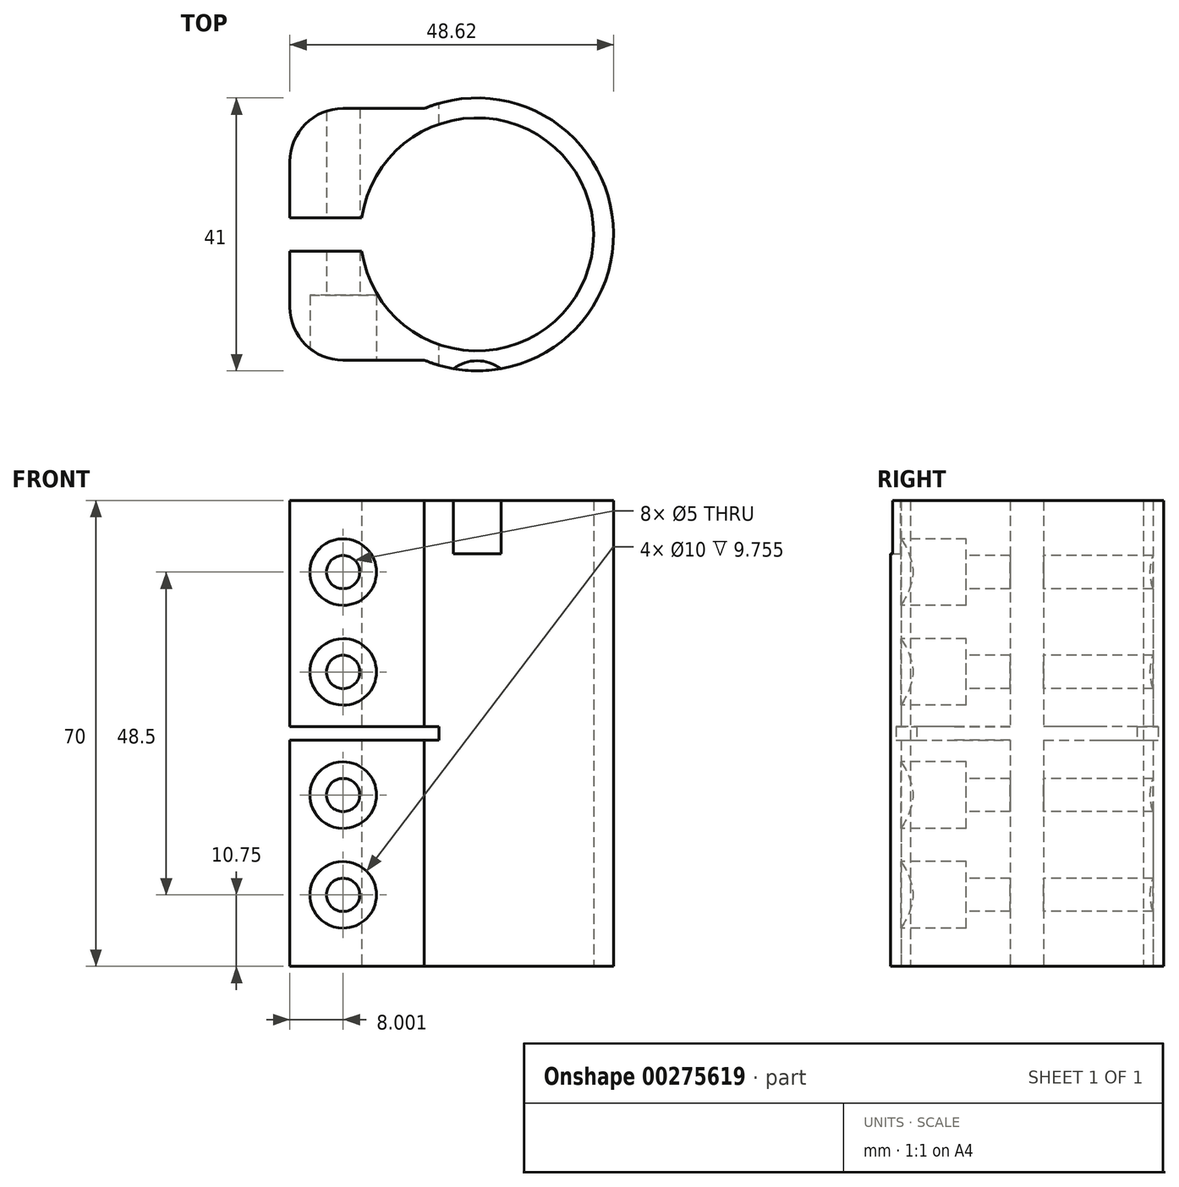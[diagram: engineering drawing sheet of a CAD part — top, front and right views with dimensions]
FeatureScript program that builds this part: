
annotation { "Feature Type Name" : "Feature", "Feature Type Description" : "" }
export const myFeature = defineFeature(function(context is Context, id is Id, definition is map)
    precondition{}
    {
        {
            var Q0;
            Q0=qCreatedBy(makeId("Top.planeOp"),FACE);
            var sketch = newSketch(context, id + "F0", { "sketchPlane" : qUnion([Q0])});
            skPoint(sketch, "E0", {"position": v(0, 0) * mm});
            skArc(sketch, "E1", {"start": v(-17.32, -2.5) * mm, "mid": v(17.5, 0) * mm, "end": v(-17.32, 2.5) * mm});
            skArc(sketch, "E2", {"start": v(-7.92, -18.9) * mm, "mid": v(20.5, 0) * mm, "end": v(-7.92, 18.9) * mm});
            skLineSegment(sketch, "E3", {"start": v(-7.92, 18.9) * mm, "end": v(-20.12, 18.9) * mm});
            skLineSegment(sketch, "E4", {"start": v(-28.12, 10.9) * mm, "end": v(-28.12, 2.5) * mm});
            skLineSegment(sketch, "E5", {"start": v(-28.12, 2.5) * mm, "end": v(-17.32, 2.5) * mm});
            skPoint(sketch, "E6.visualSharp", {"position": v(-28.12, 18.9) * mm});
            skArc(sketch, "E6.filletArc", {"start": v(-20.12, 18.9) * mm, "mid": v(-25.78, 16.57) * mm, "end": v(-28.12, 10.9) * mm});
            skLineSegment(sketch, "E7", {"start": v(0, 0) * mm, "end": v(48.76, 0) * mm, "construction": true});
            skLineSegment(sketch, "E8.MirrorCS", {"start": v(-7.92, -18.9) * mm, "end": v(-20.12, -18.9) * mm});
            skArc(sketch, "E9.MirrorCS", {"start": v(-20.12, -18.9) * mm, "mid": v(-25.78, -16.57) * mm, "end": v(-28.12, -10.9) * mm});
            skLineSegment(sketch, "E10.MirrorCS", {"start": v(-28.12, -10.9) * mm, "end": v(-28.12, -2.5) * mm});
            skLineSegment(sketch, "E11.MirrorCS", {"start": v(-28.12, -2.5) * mm, "end": v(-17.32, -2.5) * mm});
            skSolve(sketch);
        }
        {
            var Q0;
            Q0=qSketchRegion(id+"F0",true);
            extrude(context, id + "F1", {"entities" : qUnion([Q0]), "endBound" : BoundingType.SYMMETRIC, "depth" : 70 * mm});
        }
        {
            var Q0;
            Q0=makeQuery(id+"F1.opExtrude","SWEPT_FACE",FACE,{"disambiguationData":[OSD([sQuery(id+"F0.wireOp",EDGE,"E8.MirrorCS")])]});
            var sketch = newSketch(context, id + "F2", { "sketchPlane" : qUnion([Q0])});
            skPoint(sketch, "E12", {"position": v(-20.12, -24.25) * mm});
            skPoint(sketch, "E13", {"position": v(-20.12, -9.25) * mm});
            skPoint(sketch, "E14", {"position": v(-20.12, 9.25) * mm});
            skPoint(sketch, "E15", {"position": v(-20.12, 24.25) * mm});
            skSolve(sketch);
        }
        {
            var Q0;
            Q0=sQuery(id+"F2.wireOp",VERTEX,"E12");
            var Q1;
            Q1=sQuery(id+"F2.wireOp",VERTEX,"E13");
            var Q2;
            Q2=sQuery(id+"F2.wireOp",VERTEX,"E14");
            var Q3;
            Q3=sQuery(id+"F2.wireOp",VERTEX,"E15");
            var Q4;
            Q4=makeQuery(id+"F1.opExtrude","SWEPT_BODY",BODY,{"disambiguationData":[OSD([sQuery(id+"F0.wireOp",EDGE,"E1"),sQuery(id+"F0.wireOp",EDGE,"E2"),sQuery(id+"F0.wireOp",EDGE,"E3"),sQuery(id+"F0.wireOp",EDGE,"E4"),sQuery(id+"F0.wireOp",EDGE,"E5"),sQuery(id+"F0.wireOp",EDGE,"E6.filletArc"),sQuery(id+"F0.wireOp",EDGE,"E8.MirrorCS"),sQuery(id+"F0.wireOp",EDGE,"E9.MirrorCS"),sQuery(id+"F0.wireOp",EDGE,"E10.MirrorCS"),sQuery(id+"F0.wireOp",EDGE,"E11.MirrorCS")])]});
            hole(context, id + "F3", {"style" : HoleStyle.C_BORE, "endStyle" : HoleEndStyle.THROUGH, "holeDiameter" : 5 * mm, "cBoreDiameter" : 10 * mm, "cBoreDepth" : 8 * mm, "locations" : qUnion([Q0, Q1, Q2, Q3]), "scope" : qUnion([Q4]), "isTappedThrough" : true});
        }
        {
            var Q0;
            Q0=qCreatedBy(makeId("Front.planeOp"),FACE);
            var sketch = newSketch(context, id + "F4", { "sketchPlane" : qUnion([Q0])});
            skLineSegment(sketch, "E16", {"start": v(-32.28, 1) * mm, "end": v(-5.72, 1) * mm});
            skLineSegment(sketch, "E17", {"start": v(-5.72, 1) * mm, "end": v(-5.72, -1) * mm});
            skLineSegment(sketch, "E18", {"start": v(-5.72, -1) * mm, "end": v(-32.28, -1) * mm});
            skLineSegment(sketch, "E19", {"start": v(-32.28, -1) * mm, "end": v(-32.28, 1) * mm});
            skSolve(sketch);
        }
        {
            var Q0;
            Q0=qSketchRegion(id+"F4",true);
            extrude(context, id + "F5", {"entities" : qUnion([Q0]), "operationType" : NewBodyOperationType.REMOVE, "endBound" : BoundingType.SYMMETRIC, "depth" : 50 * mm});
        }
        {
            var Q0;
            Q0=makeQuery(id+"F1.opExtrude","CAP_FACE",FACE,{"disambiguationData":[OSD([sQuery(id+"F0.wireOp",EDGE,"E1"),sQuery(id+"F0.wireOp",EDGE,"E2"),sQuery(id+"F0.wireOp",EDGE,"E3"),sQuery(id+"F0.wireOp",EDGE,"E4"),sQuery(id+"F0.wireOp",EDGE,"E5"),sQuery(id+"F0.wireOp",EDGE,"E6.filletArc"),sQuery(id+"F0.wireOp",EDGE,"E8.MirrorCS"),sQuery(id+"F0.wireOp",EDGE,"E9.MirrorCS"),sQuery(id+"F0.wireOp",EDGE,"E10.MirrorCS"),sQuery(id+"F0.wireOp",EDGE,"E11.MirrorCS")])],"isStart":false});
            var sketch = newSketch(context, id + "F6", { "sketchPlane" : qUnion([Q0])});
            skPoint(sketch, "E20", {"position": v(0, -25) * mm});
            skCircle(sketch, "E21", {"center": v(0, -25) * mm, "radius": 6 * mm});
            skSolve(sketch);
        }
        {
            var Q0;
            {var subQ0=sQuery(id+"F6.wireOp",EDGE,"E21");var subQ1=makeQuery(id+"F1.opExtrude","CAP_EDGE",EDGE,{"disambiguationData":[OSD([sQuery(id+"F0.wireOp",EDGE,"E2")])],"isStart":false});var subQ2=makeQuery(id+"F6.imprint","INTERSECT",VERTEX,{"disambiguationData":[OD(0.0)],"derivedFrom":[subQ1,subQ0]});Q0=makeQuery(id+"F6.imprint","IMPRINT",FACE,{"disambiguationData":[TD([[makeQuery(id+"F6.imprint","IMPRINT",EDGE,{"disambiguationData":[TD([[subQ2,-1.0]])],"derivedFrom":subQ0}),1.0]])]});}
            var Q1;
            Q1=makeQuery(id+"FMo0qCXoM8Fg9h5_1.1.F6.imprint","IMPRINT",FACE,{"disambiguationData":[TD([[makeQuery(id+"FMo0qCXoM8Fg9h5_1.1.F6.imprint","IMPRINT",EDGE,{"derivedFrom":sQuery(id+"FMo0qCXoM8Fg9h5_1.1.F6.wireOp",EDGE,"E21")}),1.0]])]});
            var Q2;
            Q2=makeQuery(id+"FMo0qCXoM8Fg9h5_1.2.F6.imprint","IMPRINT",FACE,{"disambiguationData":[TD([[makeQuery(id+"FMo0qCXoM8Fg9h5_1.2.F6.imprint","IMPRINT",EDGE,{"derivedFrom":sQuery(id+"FMo0qCXoM8Fg9h5_1.2.F6.wireOp",EDGE,"E21")}),1.0]])]});
            var Q3;
            Q3=makeQuery(id+"FMo0qCXoM8Fg9h5_1.3.F6.imprint","IMPRINT",FACE,{"disambiguationData":[TD([[makeQuery(id+"FMo0qCXoM8Fg9h5_1.3.F6.imprint","IMPRINT",EDGE,{"derivedFrom":sQuery(id+"FMo0qCXoM8Fg9h5_1.3.F6.wireOp",EDGE,"E21")}),1.0]])]});
            var Q4;
            Q4=makeQuery(id+"FMo0qCXoM8Fg9h5_1.4.F6.imprint","IMPRINT",FACE,{"disambiguationData":[TD([[makeQuery(id+"FMo0qCXoM8Fg9h5_1.4.F6.imprint","IMPRINT",EDGE,{"derivedFrom":sQuery(id+"FMo0qCXoM8Fg9h5_1.4.F6.wireOp",EDGE,"E21")}),1.0]])]});
            extrude(context, id + "F7", {"entities" : qUnion([Q0, Q1, Q2, Q3, Q4]), "operationType" : NewBodyOperationType.REMOVE, "oppositeDirection" : true, "depth" : 8 * mm});
        }
        {
            var Q0;
            Q0=qSketchRegion(id+"F6",true);
            extrude(context, id + "F8", {"entities" : qUnion([Q0]), "operationType" : NewBodyOperationType.REMOVE, "oppositeDirection" : true, "depth" : 8 * mm});
        }
    });
